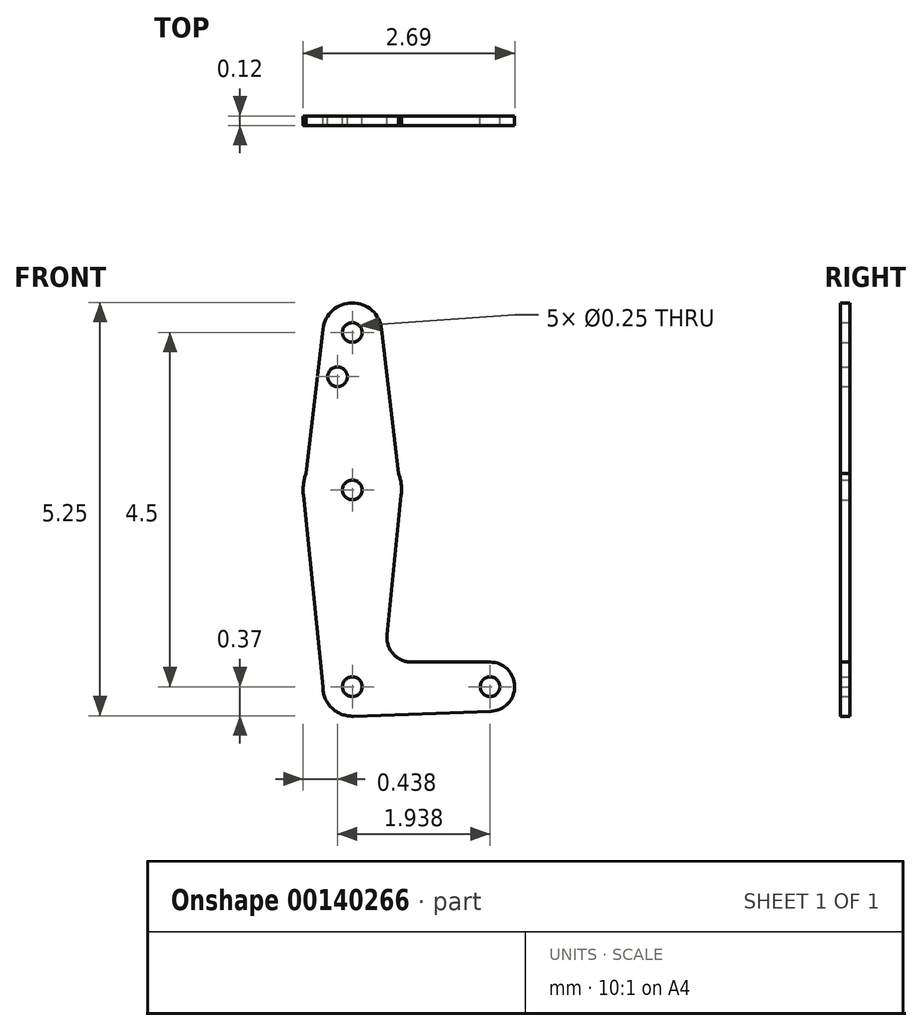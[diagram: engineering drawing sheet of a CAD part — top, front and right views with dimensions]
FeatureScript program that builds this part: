
annotation { "Feature Type Name" : "Feature", "Feature Type Description" : "" }
export const myFeature = defineFeature(function(context is Context, id is Id, definition is map)
    precondition{}
    {
        {
            var Q0;
            Q0=qCreatedBy(makeId("Front.planeOp"),FACE);
            var sketch = newSketch(context, id + "F0", { "sketchPlane" : qUnion([Q0])});
            skLineSegment(sketch, "E0", {"start": v(-4.36, 4.5) * mm, "end": v(-4.36, 0) * mm, "construction": true});
            skCircle(sketch, "E1", {"center": v(-4.36, 4.5) * mm, "radius": 0.38 * mm});
            skCircle(sketch, "E2", {"center": v(-4.36, 0) * mm, "radius": 0.38 * mm});
            skLineSegment(sketch, "E3", {"start": v(-4.36, 0) * mm, "end": v(-2.61, 0) * mm, "construction": true});
            skCircle(sketch, "E4", {"center": v(-2.61, 0) * mm, "radius": 0.31 * mm});
            skCircle(sketch, "E5", {"center": v(-4.36, 2.5) * mm, "radius": 0.62 * mm});
            skLineSegment(sketch, "E6", {"start": v(-4.35, -0.37) * mm, "end": v(-2.6, -0.31) * mm});
            skLineSegment(sketch, "E7", {"start": v(-4.74, 0) * mm, "end": v(-4.99, 2.44) * mm});
            skLineSegment(sketch, "E8", {"start": v(-3.74, 2.44) * mm, "end": v(-3.92, 0.66) * mm});
            skLineSegment(sketch, "E9", {"start": v(-4.99, 2.44) * mm, "end": v(-4.74, 4.54) * mm});
            skLineSegment(sketch, "E10", {"start": v(-3.74, 2.44) * mm, "end": v(-4, 4.54) * mm});
            skLineSegment(sketch, "E11", {"start": v(-3.61, 0.31) * mm, "end": v(-2.61, 0.31) * mm});
            skCircle(sketch, "E12", {"center": v(-4.36, 4.5) * mm, "radius": 0.12 * mm});
            skCircle(sketch, "E13", {"center": v(-4.36, 2.5) * mm, "radius": 0.12 * mm});
            skCircle(sketch, "E14", {"center": v(-4.36, 0) * mm, "radius": 0.12 * mm});
            skCircle(sketch, "E15", {"center": v(-2.61, 0) * mm, "radius": 0.12 * mm});
            skArc(sketch, "E16.filletArc", {"start": v(-3.92, 0.66) * mm, "mid": v(-3.84, 0.42) * mm, "end": v(-3.61, 0.31) * mm});
            skCircle(sketch, "E17", {"center": v(-4.55, 3.94) * mm, "radius": 0.12 * mm});
            skSolve(sketch);
        }
        {
            var Q0;
            Q0 = qSketchRegion(id + "F0", true);
            extrude(context, id + "F1", {"entities" : qUnion([Q0]), "depth" : 0.12 * mm});
        }
    });
